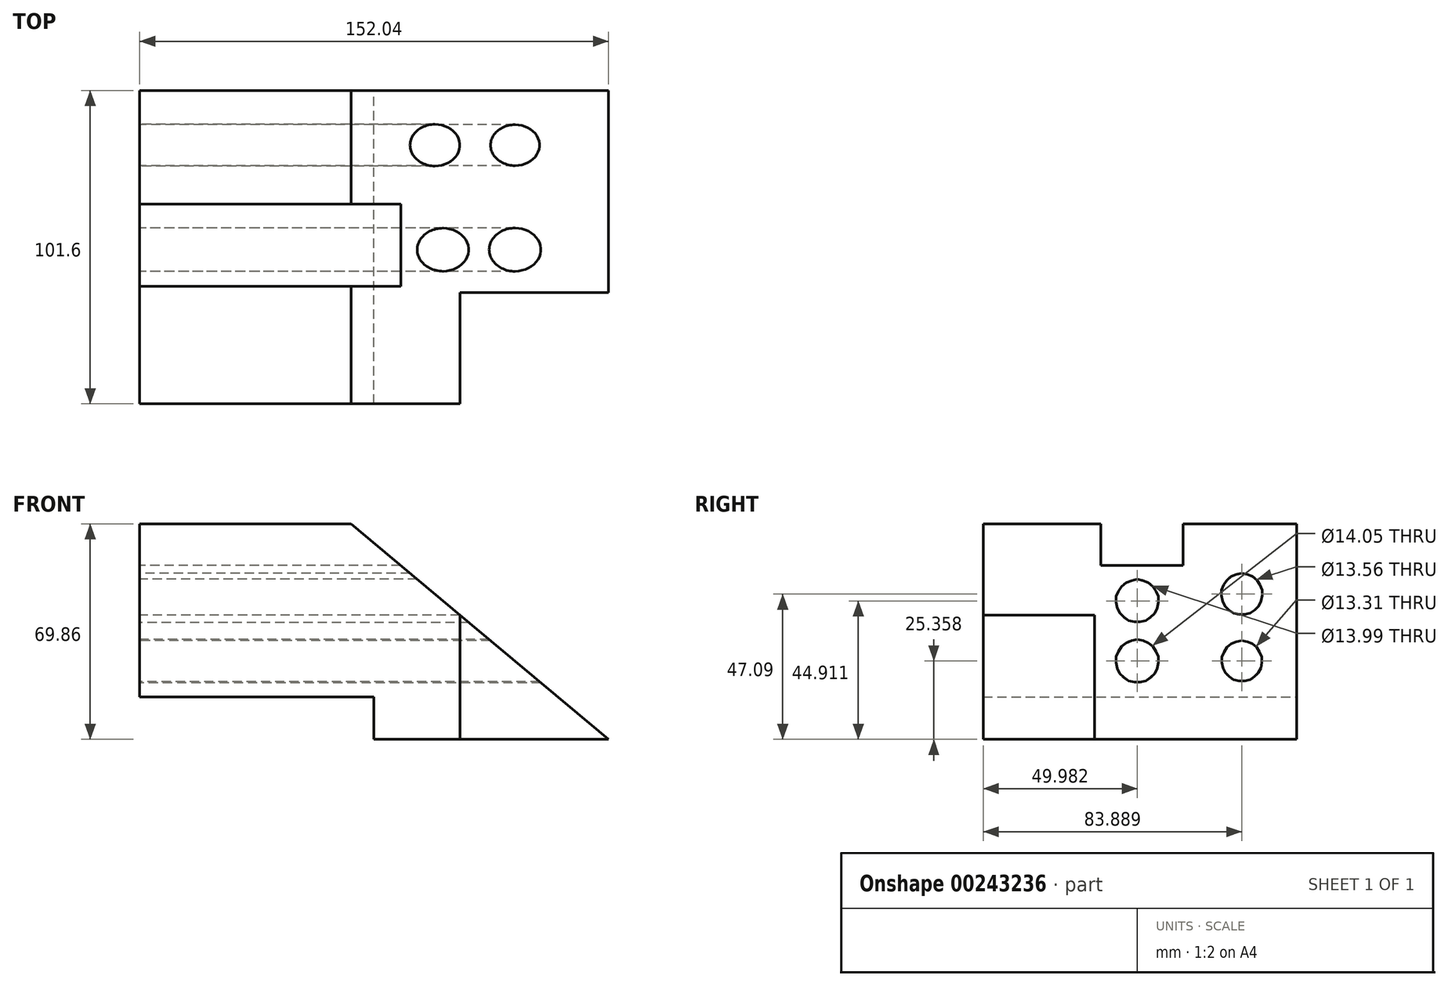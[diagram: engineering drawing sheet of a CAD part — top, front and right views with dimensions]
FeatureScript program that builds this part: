
annotation { "Feature Type Name" : "Feature", "Feature Type Description" : "" }
export const myFeature = defineFeature(function(context is Context, id is Id, definition is map)
    precondition{}
    {
        {
            var Q0;
            Q0=qCreatedBy(makeId("Front.planeOp"),FACE);
            var sketch = newSketch(context, id + "F0", { "sketchPlane" : qUnion([Q0])});
            skLineSegment(sketch, "E0", {"start": v(-75.98, 41.67) * mm, "end": v(-75.98, -18.13) * mm});
            skLineSegment(sketch, "E1", {"start": v(-75.98, -18.13) * mm, "end": v(0, -18.13) * mm});
            skLineSegment(sketch, "E2", {"start": v(0, -18.13) * mm, "end": v(0, -31.8) * mm});
            skLineSegment(sketch, "E3", {"start": v(0, -31.8) * mm, "end": v(76.06, -31.8) * mm});
            skLineSegment(sketch, "E4", {"start": v(76.06, -31.8) * mm, "end": v(-7.46, 38.06) * mm});
            skLineSegment(sketch, "E5", {"start": v(-7.46, 38.06) * mm, "end": v(-75.98, 38.06) * mm});
            skSolve(sketch);
        }
        {
            var Q0;
            {var subQ0=sQuery(id+"F0.wireOp",EDGE,"E1");Q0=makeQuery(id+"F0.imprint","IMPRINT",FACE,{"disambiguationData":[TD([[makeQuery(id+"F0.imprint","IMPRINT",EDGE,{"derivedFrom":subQ0}),1.0]])]});}
            extrude(context, id + "F1", {"entities" : qUnion([Q0]), "depth" : 101.6 * mm});
        }
        {
            var Q0;
            Q0=makeQuery(id+"F1.opExtrude","CAP_FACE",FACE,{"disambiguationData":[OSD([sQuery(id+"F0.wireOp",EDGE,"E0"),sQuery(id+"F0.wireOp",EDGE,"E1"),sQuery(id+"F0.wireOp",EDGE,"E2"),sQuery(id+"F0.wireOp",EDGE,"E3"),sQuery(id+"F0.wireOp",EDGE,"E4"),sQuery(id+"F0.wireOp",EDGE,"E5")])],"isStart":false});
            var sketch = newSketch(context, id + "F2", { "sketchPlane" : qUnion([Q0])});
            skLineSegment(sketch, "E6.bottom", {"start": v(27.9, -31.8) * mm, "end": v(90.73, -31.8) * mm});
            skLineSegment(sketch, "E6.top", {"start": v(27.9, 24.58) * mm, "end": v(90.73, 24.58) * mm});
            skLineSegment(sketch, "E6.left", {"start": v(27.9, -31.8) * mm, "end": v(27.9, 24.58) * mm});
            skLineSegment(sketch, "E6.right", {"start": v(90.73, -31.8) * mm, "end": v(90.73, 24.58) * mm});
            skSolve(sketch);
        }
        {
            var Q0;
            Q0 = qSketchRegion(id + "F2", true);
            extrude(context, id + "F3", {"entities" : qUnion([Q0]), "operationType" : NewBodyOperationType.REMOVE, "oppositeDirection" : true, "depth" : 36.07 * mm});
        }
        {
            var Q0;
            Q0=makeQuery(id+"F1.opExtrude","SWEPT_FACE",FACE,{"disambiguationData":[OSD([sQuery(id+"F0.wireOp",EDGE,"E0")])]});
            var sketch = newSketch(context, id + "F4", { "sketchPlane" : qUnion([Q0])});
            skLineSegment(sketch, "E7", {"start": v(63.46, 38.06) * mm, "end": v(63.46, 24.56) * mm});
            skLineSegment(sketch, "E8", {"start": v(63.46, 24.56) * mm, "end": v(36.8, 24.56) * mm});
            skLineSegment(sketch, "E9", {"start": v(36.8, 24.56) * mm, "end": v(36.8, 38.06) * mm});
            skLineSegment(sketch, "E10", {"start": v(36.8, 38.06) * mm, "end": v(36.8, 52.73) * mm});
            skLineSegment(sketch, "E11", {"start": v(36.8, 52.73) * mm, "end": v(63.46, 52.73) * mm});
            skLineSegment(sketch, "E12", {"start": v(63.46, 52.73) * mm, "end": v(63.46, 38.06) * mm});
            skSolve(sketch);
        }
        {
            var Q0;
            {var subQ0=sQuery(id+"F4.wireOp",EDGE,"E7");Q0=makeQuery(id+"F4.imprint","IMPRINT",FACE,{"disambiguationData":[TD([[makeQuery(id+"F4.imprint","IMPRINT",EDGE,{"derivedFrom":subQ0}),-1.0]])]});}
            var Q1;
            {var subQ0=sQuery(id+"F4.wireOp",EDGE,"E10");Q1=makeQuery(id+"F4.imprint","IMPRINT",FACE,{"disambiguationData":[TD([[makeQuery(id+"F4.imprint","IMPRINT",EDGE,{"derivedFrom":subQ0}),-1.0]])]});}
            extrude(context, id + "F5", {"entities" : qUnion([Q0, Q1]), "operationType" : NewBodyOperationType.REMOVE, "oppositeDirection" : true, "depth" : 108.7 * mm});
        }
        {
            var Q0;
            Q0=makeQuery(id+"F1.opExtrude","SWEPT_FACE",FACE,{"disambiguationData":[OSD([sQuery(id+"F0.wireOp",EDGE,"E0")])]});
            var sketch = newSketch(context, id + "F6", { "sketchPlane" : qUnion([Q0])});
            skCircle(sketch, "E13", {"center": v(51.62, -6.44) * mm, "radius": 7.03 * mm});
            skCircle(sketch, "E14", {"center": v(51.62, 13.11) * mm, "radius": 7 * mm});
            skCircle(sketch, "E15", {"center": v(17.71, -6.44) * mm, "radius": 6.66 * mm});
            skCircle(sketch, "E16", {"center": v(17.71, 15.29) * mm, "radius": 6.78 * mm});
            skSolve(sketch);
        }
        {
            var Q0;
            Q0 = qSketchRegion(id + "F6", true);
            extrude(context, id + "F7", {"entities" : qUnion([Q0]), "operationType" : NewBodyOperationType.REMOVE, "oppositeDirection" : true, "depth" : 174.75 * mm});
        }
    });
